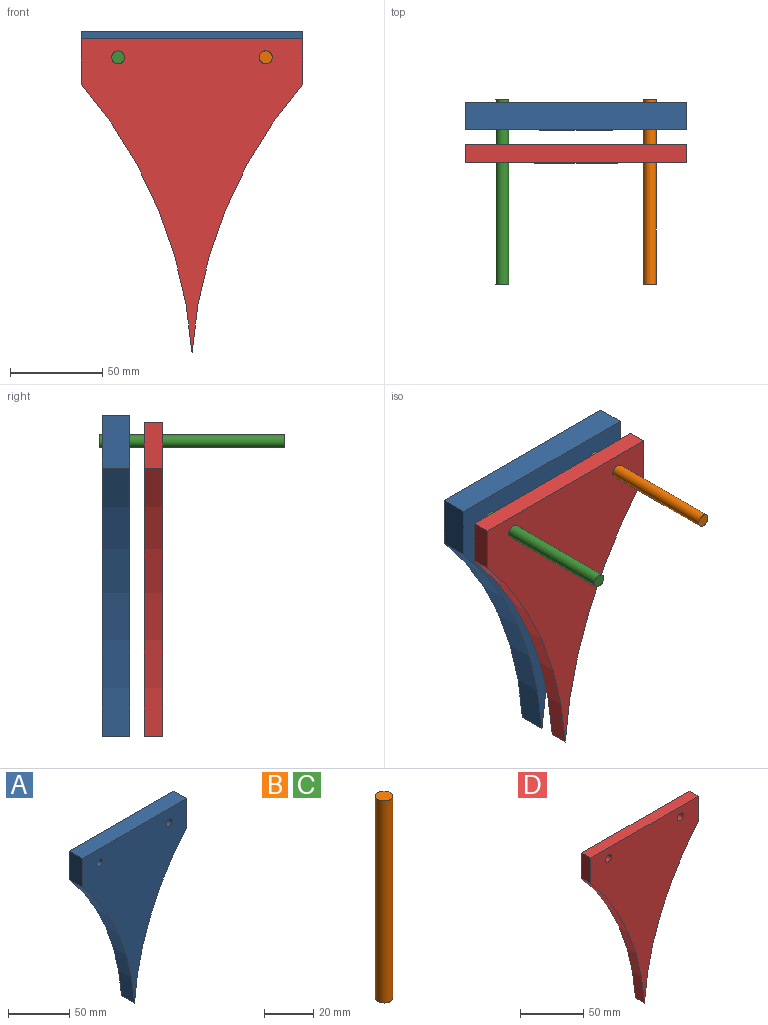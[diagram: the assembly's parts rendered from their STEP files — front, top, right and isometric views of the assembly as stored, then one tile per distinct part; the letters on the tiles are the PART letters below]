
ASSEMBLY  parts=4 mates=3
PART A: 9 faces, bbox 120x15x174 mm
  f0: plane 28.5x15mm, normal (1,0,0), area 427.5mm2, adj f1,f4,f5,f6
  f1: plane 120x15mm, normal (0,0,1), area 1800mm2, adj f0,f2,f5,f6
  f2: plane 28.5x15mm, normal (-1,0,0), area 427.5mm2, adj f1,f3,f5,f6
  f3: cylinder r=250mm len=145.5mm, axis (0,1,0), area 2401.6mm2, adj f2,f4,f5,f6
  f4: cylinder r=250mm len=145.5mm, axis (0,1,0), area 2401.6mm2, adj f0,f3,f5,f6
  f5: plane 174x120mm, normal (0,-1,0), area 9392.4mm2, adj f0,f1,f2,f3,f4,f7,f8
  f6: plane 174x120mm, normal (0,1,0), area 9392.4mm2, adj f0,f1,f2,f3,f4,f7,f8
  f7: cylinder r=3.5mm len=15mm, axis (0,1,0), area 329.9mm2, adj f5,f6
  f8: cylinder r=3.5mm len=15mm, axis (0,1,0), area 329.9mm2, adj f5,f6
PART B: 3 faces, bbox 7x7x100 mm
  f0: cylinder r=3.5mm len=100mm, axis (0,0,-1), area 2199.1mm2, adj f1,f2
  f1: plane 7x7mm, normal (0,0,1), area 38.5mm2, adj f0
  f2: plane 7x7mm, normal (0,0,-1), area 38.5mm2, adj f0
PART C: same geometry as B
PART D: 9 faces, bbox 120x10x170 mm
  f0: plane 24.5x10mm, normal (1,0,0), area 245mm2, adj f1,f4,f5,f6
  f1: plane 120x10mm, normal (0,0,1), area 1200mm2, adj f0,f2,f5,f6
  f2: plane 24.5x10mm, normal (-1,0,0), area 245mm2, adj f1,f3,f5,f6
  f3: cylinder r=250mm len=145.5mm, axis (0,1,0), area 1601.1mm2, adj f2,f4,f5,f6
  f4: cylinder r=250mm len=145.5mm, axis (0,1,0), area 1601.1mm2, adj f0,f3,f5,f6
  f5: plane 170x120mm, normal (0,-1,0), area 8912.4mm2, adj f0,f1,f2,f3,f4,f7,f8
  f6: plane 170x120mm, normal (0,1,0), area 8912.4mm2, adj f0,f1,f2,f3,f4,f7,f8
  f7: cylinder r=3.5mm len=10mm, axis (0,1,0), area 219.9mm2, adj f5,f6
  f8: cylinder r=3.5mm len=10mm, axis (0,1,0), area 219.9mm2, adj f5,f6
PLACE A t=(-13.96,-38.24,4.87)mm
PLACE B rot(axis=(-1,0,0),90deg) t=(86.04,-136.94,-9.13)mm
PLACE C rot(axis=(-1,0,0),90deg) t=(6.04,-137.04,-9.13)mm
PLACE D rot(axis=(1,0,0),0deg) t=(-13.96,-61.14,0.87)mm
MATE slider D.f7 <-> B.f0  axis (0,1,0) through (86.04,-61.14,-9.13)mm
MATE slider C.f0 <-> A.f8  axis (0,1,0) through (6.04,-37.04,-9.13)mm
MATE slider B.f0 <-> A.f7  axis (0,1,0) through (86.04,-36.94,-9.13)mm
